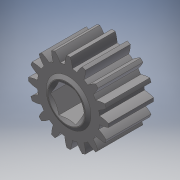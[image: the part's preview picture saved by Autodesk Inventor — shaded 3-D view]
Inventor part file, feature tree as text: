
AUTODESK INVENTOR PART (.ipt)
format: ipt  version: 2018 (Build 220112000, 112)  size: 378,880 bytes
history: native  units: in
note: dims shown in document units (in); Inventor stores cm internally (conversion verified against a paired STEP export)
features: other x3, direct_edit x2, plane x2, extrude x2, boolean_combine x2, move_body x2, sketch x1, pattern_circular x1
ambient origin geometry x8: Origin, YZ Plane, XZ Plane, XY Plane, X Axis, Y Axis, Z Axis, Center Point
bodies: Solid2 (feature_tree), Solid1 (feature_tree)
feature tree (15):
  other  "SW-GEAR-20DP-14T.ipt"
  sketch  "Sketch1"  dims[d0=0.3937in d1=0.8in d2=0.1125in d3=0.0in d4=-0.113in d5=0.0in d6=1.0in d7=0.0in d8=1.0in d9=0.0in d10=6.2992in d11=360.0deg d14=-0.575in d15=0.0in d16=0.0in d17=0.2in]
  direct_edit  "Direct Edit1"
  plane  "Work Plane2"
  direct_edit  "Direct Edit2"
  extrude  "Extrusion1"  Depth=0.3937in
  extrude  "Extrusion2"  Depth=0.3937in
  boolean_combine  "Combine1"
  pattern_circular  "Circular Pattern1"  [2 undecoded]
  boolean_combine  "Combine2"
  plane  "Work Plane MID-TOOTH"
  other  "Toughbox_d08::SW-GEAR-20DP-14T.ipt"
  other  "TaggingFeature1"
  move_body  "Move1"
  move_body  "Move2"
note: 2 required parameter values undecoded (feature->parameter linkage not recoverable at this tier; creation-order binding heuristic only, values carry confidence <= 0.55)
